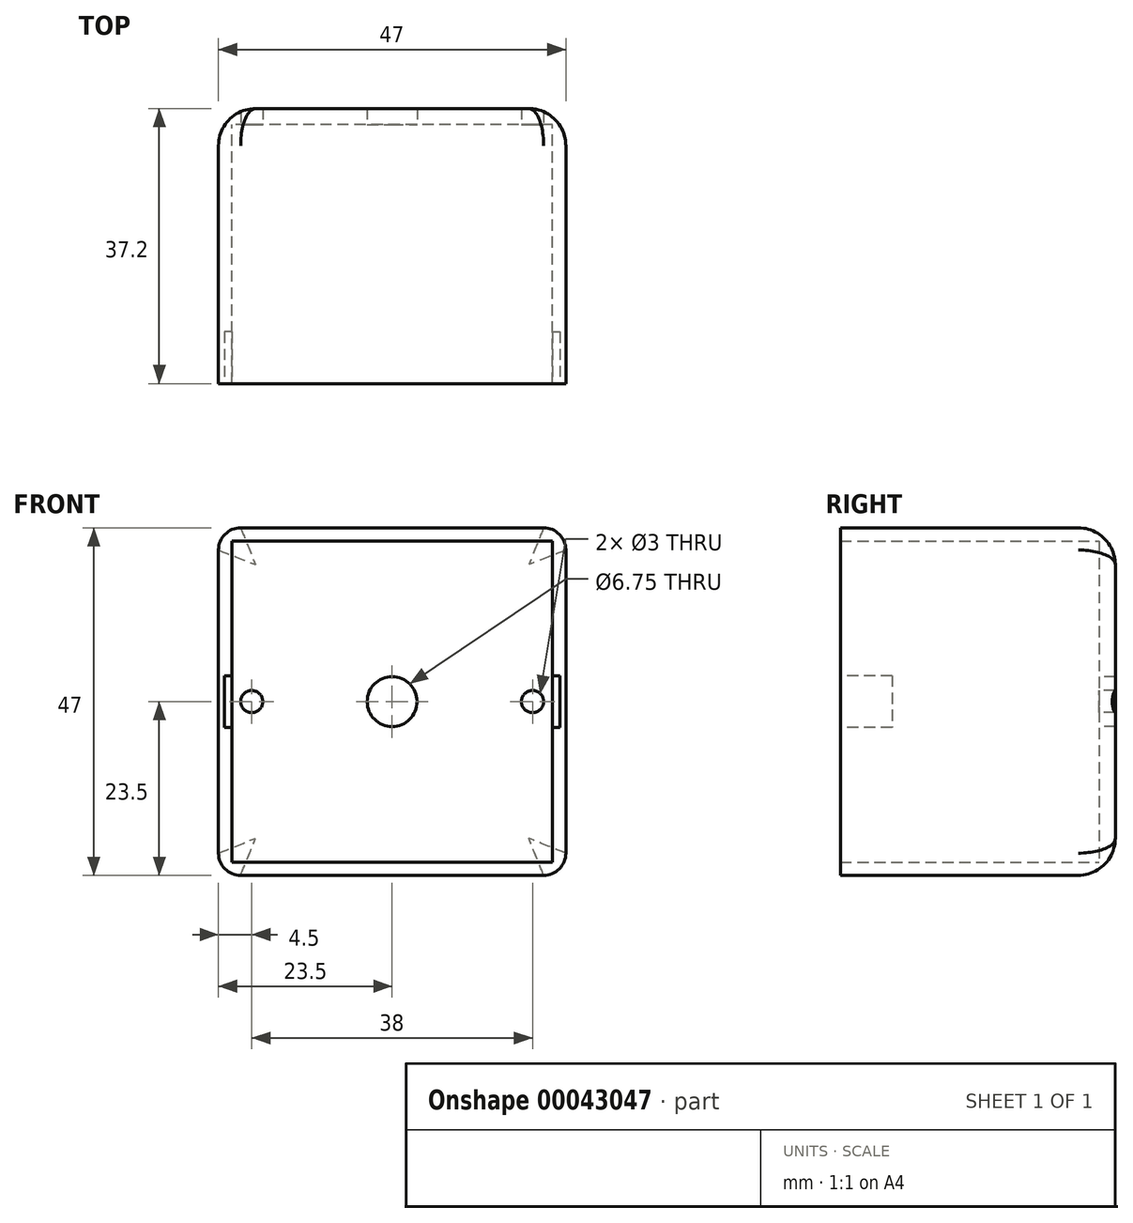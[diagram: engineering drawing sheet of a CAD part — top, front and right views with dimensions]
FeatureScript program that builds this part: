
annotation { "Feature Type Name" : "Feature", "Feature Type Description" : "" }
export const myFeature = defineFeature(function(context is Context, id is Id, definition is map)
    precondition{}
    {
        {
            var Q0;
            Q0=qCreatedBy(makeId("Front.planeOp"),FACE);
            var sketch = newSketch(context, id + "F0", { "sketchPlane" : qUnion([Q0])});
            skLineSegment(sketch, "E0.rect.bottom", {"start": v(23.5, 23.5) * mm, "end": v(-23.5, 23.5) * mm});
            skLineSegment(sketch, "E0.rect.top", {"start": v(23.5, -23.5) * mm, "end": v(-23.5, -23.5) * mm});
            skLineSegment(sketch, "E0.rect.left", {"start": v(23.5, 23.5) * mm, "end": v(23.5, -23.5) * mm});
            skLineSegment(sketch, "E0.rect.right", {"start": v(-23.5, 23.5) * mm, "end": v(-23.5, -23.5) * mm});
            skPoint(sketch, "E0.rect.middle", {"position": v(0, 0) * mm});
            skLineSegment(sketch, "E1.0", {"start": v(21.7, 21.7) * mm, "end": v(21.7, -21.7) * mm});
            skLineSegment(sketch, "E1.1", {"start": v(21.7, 21.7) * mm, "end": v(-21.7, 21.7) * mm});
            skLineSegment(sketch, "E1.2", {"start": v(-21.7, 21.7) * mm, "end": v(-21.7, -21.7) * mm});
            skLineSegment(sketch, "E1.3", {"start": v(21.7, -21.7) * mm, "end": v(-21.7, -21.7) * mm});
            skSolve(sketch);
        }
        {
            var Q0;
            Q0=makeQuery(id+"F0.imprint","IMPRINT",FACE,{"disambiguationData":[TD([[makeQuery(id+"F0.imprint","IMPRINT",EDGE,{"derivedFrom":sQuery(id+"F0.wireOp",EDGE,"E0.rect.bottom")}),1.0]])]});
            extrude(context, id + "F1", {"entities" : qUnion([Q0]), "depth" : 35 * mm});
        }
        {
            var Q0;
            Q0=makeQuery(id+"F1.opExtrude","CAP_FACE",FACE,{"disambiguationData":[OSD([sQuery(id+"F0.wireOp",EDGE,"E0.rect.bottom"),sQuery(id+"F0.wireOp",EDGE,"E0.rect.top"),sQuery(id+"F0.wireOp",EDGE,"E0.rect.left"),sQuery(id+"F0.wireOp",EDGE,"E0.rect.right"),sQuery(id+"F0.wireOp",EDGE,"E1.0"),sQuery(id+"F0.wireOp",EDGE,"E1.1"),sQuery(id+"F0.wireOp",EDGE,"E1.2"),sQuery(id+"F0.wireOp",EDGE,"E1.3")])],"isStart":false});
            var sketch = newSketch(context, id + "F2", { "sketchPlane" : qUnion([Q0])});
            skLineSegment(sketch, "E2.bottom", {"start": v(-21.7, 3.5) * mm, "end": v(-22.7, 3.5) * mm});
            skLineSegment(sketch, "E2.top", {"start": v(-21.7, -3.5) * mm, "end": v(-22.7, -3.5) * mm});
            skLineSegment(sketch, "E2.left", {"start": v(-21.7, 3.5) * mm, "end": v(-21.7, -3.5) * mm});
            skLineSegment(sketch, "E2.right", {"start": v(-22.7, 3.5) * mm, "end": v(-22.7, -3.5) * mm});
            skLineSegment(sketch, "E3.MirrorCS", {"start": v(21.7, 3.5) * mm, "end": v(21.7, -3.5) * mm});
            skLineSegment(sketch, "E4.MirrorCS", {"start": v(21.7, -3.5) * mm, "end": v(22.7, -3.5) * mm});
            skLineSegment(sketch, "E5.MirrorCS", {"start": v(22.7, 3.5) * mm, "end": v(22.7, -3.5) * mm});
            skLineSegment(sketch, "E6.MirrorCS", {"start": v(21.7, 3.5) * mm, "end": v(22.7, 3.5) * mm});
            skSolve(sketch);
        }
        {
            var Q0;
            Q0 = qSketchRegion(id + "F2", true);
            extrude(context, id + "F3", {"entities" : qUnion([Q0]), "operationType" : NewBodyOperationType.REMOVE, "oppositeDirection" : true, "depth" : 7 * mm});
        }
        {
            var Q0;
            Q0=makeQuery(id+"F1.opExtrude","CAP_FACE",FACE,{"disambiguationData":[OSD([sQuery(id+"F0.wireOp",EDGE,"E0.rect.bottom"),sQuery(id+"F0.wireOp",EDGE,"E0.rect.top"),sQuery(id+"F0.wireOp",EDGE,"E0.rect.left"),sQuery(id+"F0.wireOp",EDGE,"E0.rect.right"),sQuery(id+"F0.wireOp",EDGE,"E1.0"),sQuery(id+"F0.wireOp",EDGE,"E1.1"),sQuery(id+"F0.wireOp",EDGE,"E1.2"),sQuery(id+"F0.wireOp",EDGE,"E1.3")])],"isStart":true});
            var sketch = newSketch(context, id + "F4", { "sketchPlane" : qUnion([Q0])});
            skLineSegment(sketch, "E7.bottom", {"start": v(23.5, 23.5) * mm, "end": v(-23.5, 23.5) * mm});
            skLineSegment(sketch, "E7.top", {"start": v(23.5, -23.5) * mm, "end": v(-23.5, -23.5) * mm});
            skLineSegment(sketch, "E7.left", {"start": v(23.5, 23.5) * mm, "end": v(23.5, -23.5) * mm});
            skLineSegment(sketch, "E7.right", {"start": v(-23.5, 23.5) * mm, "end": v(-23.5, -23.5) * mm});
            skCircle(sketch, "E8", {"center": v(19, 0) * mm, "radius": 1.5 * mm});
            skCircle(sketch, "E9.MirrorC", {"center": v(-19, 0) * mm, "radius": 1.5 * mm});
            skCircle(sketch, "E10", {"center": v(0, 0) * mm, "radius": 3.38 * mm});
            skSolve(sketch);
        }
        {
            var Q0;
            Q0 = qSketchRegion(id + "F4", true);
            extrude(context, id + "F5", {"entities" : qUnion([Q0]), "operationType" : NewBodyOperationType.ADD, "depth" : 2.2 * mm});
        }
        {
            var Q0;
            Q0=makeQuery(id+"F5.boolean.opBoolean","MERGE",EDGE,{"derivedFrom":[makeQuery(id+"F1.opExtrude","SWEPT_EDGE",EDGE,{"disambiguationData":[OSD([sQuery(id+"F0.wireOp",EDGE,"E0.rect.bottom"),sQuery(id+"F0.wireOp",EDGE,"E0.rect.right")])]}),makeQuery(id+"F5.opExtrude","SWEPT_EDGE",EDGE,{"disambiguationData":[OSD([sQuery(id+"F4.wireOp",EDGE,"E7.bottom"),sQuery(id+"F4.wireOp",EDGE,"E7.left")])]})]});
            var Q1;
            Q1=makeQuery(id+"F5.boolean.opBoolean","MERGE",EDGE,{"derivedFrom":[makeQuery(id+"F1.opExtrude","SWEPT_EDGE",EDGE,{"disambiguationData":[OSD([sQuery(id+"F0.wireOp",EDGE,"E0.rect.top"),sQuery(id+"F0.wireOp",EDGE,"E0.rect.right")])]}),makeQuery(id+"F5.opExtrude","SWEPT_EDGE",EDGE,{"disambiguationData":[OSD([sQuery(id+"F4.wireOp",EDGE,"E7.top"),sQuery(id+"F4.wireOp",EDGE,"E7.left")])]})]});
            var Q2;
            Q2=makeQuery(id+"F5.boolean.opBoolean","MERGE",EDGE,{"derivedFrom":[makeQuery(id+"F1.opExtrude","SWEPT_EDGE",EDGE,{"disambiguationData":[OSD([sQuery(id+"F0.wireOp",EDGE,"E0.rect.top"),sQuery(id+"F0.wireOp",EDGE,"E0.rect.left")])]}),makeQuery(id+"F5.opExtrude","SWEPT_EDGE",EDGE,{"disambiguationData":[OSD([sQuery(id+"F4.wireOp",EDGE,"E7.top"),sQuery(id+"F4.wireOp",EDGE,"E7.right")])]})]});
            var Q3;
            Q3=makeQuery(id+"F5.boolean.opBoolean","MERGE",EDGE,{"derivedFrom":[makeQuery(id+"F1.opExtrude","SWEPT_EDGE",EDGE,{"disambiguationData":[OSD([sQuery(id+"F0.wireOp",EDGE,"E0.rect.bottom"),sQuery(id+"F0.wireOp",EDGE,"E0.rect.left")])]}),makeQuery(id+"F5.opExtrude","SWEPT_EDGE",EDGE,{"disambiguationData":[OSD([sQuery(id+"F4.wireOp",EDGE,"E7.bottom"),sQuery(id+"F4.wireOp",EDGE,"E7.right")])]})]});
            fillet(context, id + "F6", {"entities" : qUnion([Q0, Q1, Q2, Q3]), "radius" : 3 * mm, "tangentPropagation" : true, "allowEdgeOverflow" : false});
        }
        {
            var Q0;
            Q0=makeQuery(id+"F5.opExtrude","CAP_EDGE",EDGE,{"disambiguationData":[OSD([sQuery(id+"F4.wireOp",EDGE,"E7.bottom")])],"isStart":false});
            var Q1;
            {var subQ0=sQuery(id+"F4.wireOp",EDGE,"E7.bottom");var subQ1=sQuery(id+"F4.wireOp",EDGE,"E7.right");Q1=makeQuery(id+"F6.opFillet","BLEND_EDGE",EDGE,{"blendedFrom":[makeQuery(id+"F5.boolean.opBoolean","MERGE",EDGE,{"derivedFrom":[makeQuery(id+"F1.opExtrude","SWEPT_EDGE",EDGE,{"disambiguationData":[OSD([sQuery(id+"F0.wireOp",EDGE,"E0.rect.bottom"),sQuery(id+"F0.wireOp",EDGE,"E0.rect.left")])]}),makeQuery(id+"F5.opExtrude","SWEPT_EDGE",EDGE,{"disambiguationData":[OSD([subQ0,subQ1])]})]}),makeQuery(id+"F5.opExtrude","CAP_FACE",FACE,{"disambiguationData":[OSD([subQ0,sQuery(id+"F4.wireOp",EDGE,"E7.top"),sQuery(id+"F4.wireOp",EDGE,"E7.left"),subQ1,sQuery(id+"F4.wireOp",EDGE,"E8"),sQuery(id+"F4.wireOp",EDGE,"E9.MirrorC"),sQuery(id+"F4.wireOp",EDGE,"E10")])],"isStart":false})],"blendedInto":[makeQuery(id+"F5.opExtrude","CAP_FACE",FACE,{"disambiguationData":[OSD([subQ0,sQuery(id+"F4.wireOp",EDGE,"E7.top"),sQuery(id+"F4.wireOp",EDGE,"E7.left"),subQ1,sQuery(id+"F4.wireOp",EDGE,"E8"),sQuery(id+"F4.wireOp",EDGE,"E9.MirrorC"),sQuery(id+"F4.wireOp",EDGE,"E10")])],"isStart":false})]});}
            var Q2;
            Q2=makeQuery(id+"F5.opExtrude","CAP_EDGE",EDGE,{"disambiguationData":[OSD([sQuery(id+"F4.wireOp",EDGE,"E7.right")])],"isStart":false});
            var Q3;
            {var subQ0=sQuery(id+"F4.wireOp",EDGE,"E7.top");var subQ1=sQuery(id+"F4.wireOp",EDGE,"E7.right");Q3=makeQuery(id+"F6.opFillet","BLEND_EDGE",EDGE,{"blendedFrom":[makeQuery(id+"F5.boolean.opBoolean","MERGE",EDGE,{"derivedFrom":[makeQuery(id+"F1.opExtrude","SWEPT_EDGE",EDGE,{"disambiguationData":[OSD([sQuery(id+"F0.wireOp",EDGE,"E0.rect.top"),sQuery(id+"F0.wireOp",EDGE,"E0.rect.left")])]}),makeQuery(id+"F5.opExtrude","SWEPT_EDGE",EDGE,{"disambiguationData":[OSD([subQ0,subQ1])]})]}),makeQuery(id+"F5.opExtrude","CAP_FACE",FACE,{"disambiguationData":[OSD([sQuery(id+"F4.wireOp",EDGE,"E7.bottom"),subQ0,sQuery(id+"F4.wireOp",EDGE,"E7.left"),subQ1,sQuery(id+"F4.wireOp",EDGE,"E8"),sQuery(id+"F4.wireOp",EDGE,"E9.MirrorC"),sQuery(id+"F4.wireOp",EDGE,"E10")])],"isStart":false})],"blendedInto":[makeQuery(id+"F5.opExtrude","CAP_FACE",FACE,{"disambiguationData":[OSD([sQuery(id+"F4.wireOp",EDGE,"E7.bottom"),subQ0,sQuery(id+"F4.wireOp",EDGE,"E7.left"),subQ1,sQuery(id+"F4.wireOp",EDGE,"E8"),sQuery(id+"F4.wireOp",EDGE,"E9.MirrorC"),sQuery(id+"F4.wireOp",EDGE,"E10")])],"isStart":false})]});}
            var Q4;
            Q4=makeQuery(id+"F5.opExtrude","CAP_EDGE",EDGE,{"disambiguationData":[OSD([sQuery(id+"F4.wireOp",EDGE,"E7.top")])],"isStart":false});
            var Q5;
            {var subQ0=sQuery(id+"F4.wireOp",EDGE,"E7.top");var subQ1=sQuery(id+"F4.wireOp",EDGE,"E7.left");Q5=makeQuery(id+"F6.opFillet","BLEND_EDGE",EDGE,{"blendedFrom":[makeQuery(id+"F5.boolean.opBoolean","MERGE",EDGE,{"derivedFrom":[makeQuery(id+"F1.opExtrude","SWEPT_EDGE",EDGE,{"disambiguationData":[OSD([sQuery(id+"F0.wireOp",EDGE,"E0.rect.top"),sQuery(id+"F0.wireOp",EDGE,"E0.rect.right")])]}),makeQuery(id+"F5.opExtrude","SWEPT_EDGE",EDGE,{"disambiguationData":[OSD([subQ0,subQ1])]})]}),makeQuery(id+"F5.opExtrude","CAP_FACE",FACE,{"disambiguationData":[OSD([sQuery(id+"F4.wireOp",EDGE,"E7.bottom"),subQ0,subQ1,sQuery(id+"F4.wireOp",EDGE,"E7.right"),sQuery(id+"F4.wireOp",EDGE,"E8"),sQuery(id+"F4.wireOp",EDGE,"E9.MirrorC"),sQuery(id+"F4.wireOp",EDGE,"E10")])],"isStart":false})],"blendedInto":[makeQuery(id+"F5.opExtrude","CAP_FACE",FACE,{"disambiguationData":[OSD([sQuery(id+"F4.wireOp",EDGE,"E7.bottom"),subQ0,subQ1,sQuery(id+"F4.wireOp",EDGE,"E7.right"),sQuery(id+"F4.wireOp",EDGE,"E8"),sQuery(id+"F4.wireOp",EDGE,"E9.MirrorC"),sQuery(id+"F4.wireOp",EDGE,"E10")])],"isStart":false})]});}
            var Q6;
            Q6=makeQuery(id+"F5.opExtrude","CAP_EDGE",EDGE,{"disambiguationData":[OSD([sQuery(id+"F4.wireOp",EDGE,"E7.left")])],"isStart":false});
            var Q7;
            {var subQ0=sQuery(id+"F4.wireOp",EDGE,"E7.bottom");var subQ1=sQuery(id+"F4.wireOp",EDGE,"E7.left");Q7=makeQuery(id+"F6.opFillet","BLEND_EDGE",EDGE,{"blendedFrom":[makeQuery(id+"F5.boolean.opBoolean","MERGE",EDGE,{"derivedFrom":[makeQuery(id+"F1.opExtrude","SWEPT_EDGE",EDGE,{"disambiguationData":[OSD([sQuery(id+"F0.wireOp",EDGE,"E0.rect.bottom"),sQuery(id+"F0.wireOp",EDGE,"E0.rect.right")])]}),makeQuery(id+"F5.opExtrude","SWEPT_EDGE",EDGE,{"disambiguationData":[OSD([subQ0,subQ1])]})]}),makeQuery(id+"F5.opExtrude","CAP_FACE",FACE,{"disambiguationData":[OSD([subQ0,sQuery(id+"F4.wireOp",EDGE,"E7.top"),subQ1,sQuery(id+"F4.wireOp",EDGE,"E7.right"),sQuery(id+"F4.wireOp",EDGE,"E8"),sQuery(id+"F4.wireOp",EDGE,"E9.MirrorC"),sQuery(id+"F4.wireOp",EDGE,"E10")])],"isStart":false})],"blendedInto":[makeQuery(id+"F5.opExtrude","CAP_FACE",FACE,{"disambiguationData":[OSD([subQ0,sQuery(id+"F4.wireOp",EDGE,"E7.top"),subQ1,sQuery(id+"F4.wireOp",EDGE,"E7.right"),sQuery(id+"F4.wireOp",EDGE,"E8"),sQuery(id+"F4.wireOp",EDGE,"E9.MirrorC"),sQuery(id+"F4.wireOp",EDGE,"E10")])],"isStart":false})]});}
            fillet(context, id + "F7", {"entities" : qUnion([Q0, Q1, Q2, Q3, Q4, Q5, Q6, Q7]), "radius" : 5 * mm, "tangentPropagation" : true, "allowEdgeOverflow" : false});
        }
    });
